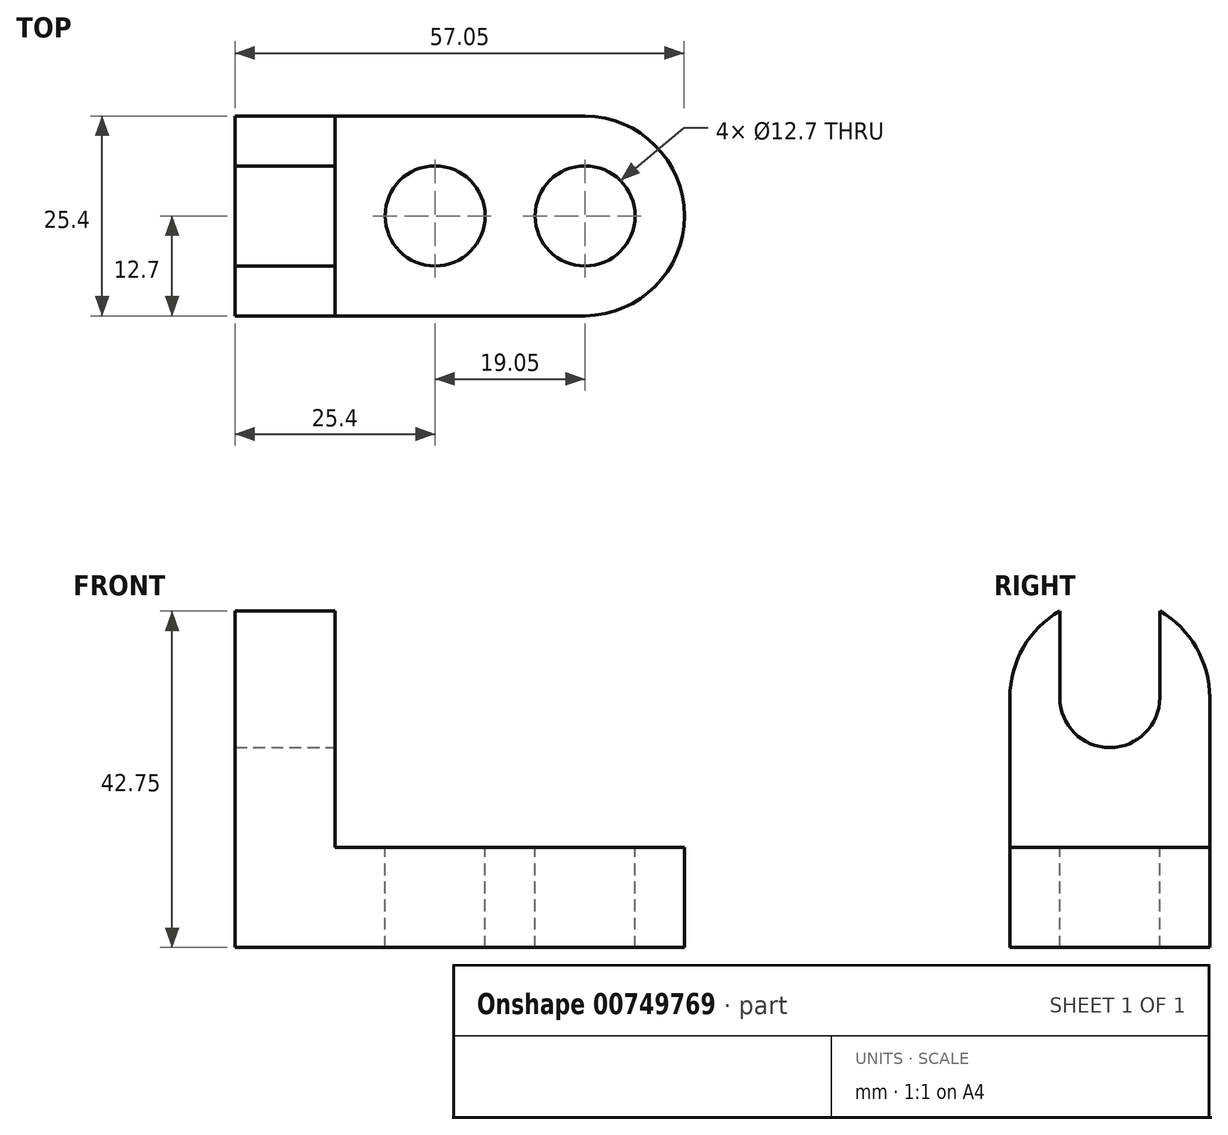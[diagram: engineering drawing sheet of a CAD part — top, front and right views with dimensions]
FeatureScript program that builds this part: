
annotation { "Feature Type Name" : "Feature", "Feature Type Description" : "" }
export const myFeature = defineFeature(function(context is Context, id is Id, definition is map)
    precondition{}
    {
        {
            var Q0;
            Q0=qCreatedBy(makeId("Front.planeOp"),FACE);
            var sketch = newSketch(context, id + "F0", { "sketchPlane" : qUnion([Q0])});
            skLineSegment(sketch, "E0", {"start": v(0, 0) * mm, "end": v(57.15, 0) * mm});
            skLineSegment(sketch, "E1", {"start": v(57.15, 0) * mm, "end": v(57.15, 12.7) * mm});
            skLineSegment(sketch, "E2", {"start": v(57.15, 12.7) * mm, "end": v(12.7, 12.7) * mm});
            skLineSegment(sketch, "E3", {"start": v(12.7, 12.7) * mm, "end": v(12.7, 44.45) * mm});
            skLineSegment(sketch, "E4", {"start": v(12.7, 44.45) * mm, "end": v(0, 44.45) * mm});
            skLineSegment(sketch, "E5", {"start": v(0, 44.45) * mm, "end": v(0, 0) * mm});
            skSolve(sketch);
        }
        {
            var Q0;
            Q0=makeQuery(id+"F0.imprint","IMPRINT",FACE,{"disambiguationData":[TD([[makeQuery(id+"F0.imprint","IMPRINT",EDGE,{"derivedFrom":sQuery(id+"F0.wireOp",EDGE,"E0")}),1.0]])]});
            extrude(context, id + "F1", {"entities" : qUnion([Q0]), "depth" : 25.4 * mm, "offsetDistance" : 25.4 * mm});
        }
        {
            var Q0;
            Q0=makeQuery(id+"F1.opExtrude","SWEPT_FACE",FACE,{"disambiguationData":[OSD([sQuery(id+"F0.wireOp",EDGE,"E2")])]});
            var sketch = newSketch(context, id + "F2", { "sketchPlane" : qUnion([Q0])});
            skLineSegment(sketch, "E6", {"start": v(44.45, 0) * mm, "end": v(44.45, -25.4) * mm});
            skLineSegment(sketch, "E7", {"start": v(25.4, 0) * mm, "end": v(25.4, -25.4) * mm});
            skCircle(sketch, "E8", {"center": v(25.4, -12.7) * mm, "radius": 6.35 * mm});
            skCircle(sketch, "E9", {"center": v(44.45, -12.7) * mm, "radius": 6.35 * mm});
            skLineSegment(sketch, "E10", {"start": v(25.4, -6.35) * mm, "end": v(44.45, -6.35) * mm});
            skLineSegment(sketch, "E11", {"start": v(25.4, -19.05) * mm, "end": v(44.45, -19.05) * mm});
            skArc(sketch, "E12", {"start": v(44.45, -25.4) * mm, "mid": v(57.05, -12.7) * mm, "end": v(44.45, 0) * mm});
            skSolve(sketch);
        }
        {
            var Q0;
            {var subQ0=sQuery(id+"F2.wireOp",EDGE,"E8");var subQ1=sQuery(id+"F2.wireOp",EDGE,"E7");var subQ2=makeQuery(id+"F2.imprint","INTERSECT",VERTEX,{"derivedFrom":[subQ1,subQ0,sQuery(id+"F2.wireOp",EDGE,"E10")]});Q0=makeQuery(id+"F2.imprint","IMPRINT",FACE,{"disambiguationData":[TD([[makeQuery(id+"F2.imprint","IMPRINT",EDGE,{"disambiguationData":[TD([[subQ2,-1.0]])],"derivedFrom":subQ1}),-1.0]])]});}
            var Q1;
            {var subQ0=sQuery(id+"F2.wireOp",EDGE,"E8");var subQ1=sQuery(id+"F2.wireOp",EDGE,"E7");var subQ2=makeQuery(id+"F2.imprint","INTERSECT",VERTEX,{"derivedFrom":[subQ1,subQ0,sQuery(id+"F2.wireOp",EDGE,"E10")]});Q1=makeQuery(id+"F2.imprint","IMPRINT",FACE,{"disambiguationData":[TD([[makeQuery(id+"F2.imprint","IMPRINT",EDGE,{"disambiguationData":[TD([[subQ2,-1.0]])],"derivedFrom":subQ1}),1.0]])]});}
            var Q2;
            {var subQ0=sQuery(id+"F2.wireOp",EDGE,"E9");var subQ1=sQuery(id+"F2.wireOp",EDGE,"E6");var subQ2=makeQuery(id+"F2.imprint","INTERSECT",VERTEX,{"derivedFrom":[subQ1,subQ0,sQuery(id+"F2.wireOp",EDGE,"E10")]});Q2=makeQuery(id+"F2.imprint","IMPRINT",FACE,{"disambiguationData":[TD([[makeQuery(id+"F2.imprint","IMPRINT",EDGE,{"disambiguationData":[TD([[subQ2,-1.0]])],"derivedFrom":subQ1}),-1.0]])]});}
            var Q3;
            {var subQ0=sQuery(id+"F2.wireOp",EDGE,"E9");var subQ1=sQuery(id+"F2.wireOp",EDGE,"E6");var subQ2=makeQuery(id+"F2.imprint","INTERSECT",VERTEX,{"derivedFrom":[subQ1,subQ0,sQuery(id+"F2.wireOp",EDGE,"E10")]});Q3=makeQuery(id+"F2.imprint","IMPRINT",FACE,{"disambiguationData":[TD([[makeQuery(id+"F2.imprint","IMPRINT",EDGE,{"disambiguationData":[TD([[subQ2,-1.0]])],"derivedFrom":subQ1}),1.0]])]});}
            var Q4;
            {var subQ0=sQuery(id+"F2.wireOp",EDGE,"E12");Q4=makeQuery(id+"F2.imprint","IMPRINT",FACE,{"disambiguationData":[TD([[makeQuery(id+"F2.imprint","IMPRINT",EDGE,{"derivedFrom":subQ0}),-1.0]])]});}
            extrude(context, id + "F3", {"entities" : qUnion([Q0, Q1, Q2, Q3, Q4]), "operationType" : NewBodyOperationType.REMOVE, "endBound" : BoundingType.THROUGH_ALL, "oppositeDirection" : true, "depth" : 25.4 * mm, "offsetDistance" : 25.4 * mm});
        }
        {
            var Q0;
            Q0=makeQuery(id+"F1.opExtrude","SWEPT_FACE",FACE,{"disambiguationData":[OSD([sQuery(id+"F0.wireOp",EDGE,"E3")])]});
            var sketch = newSketch(context, id + "F4", { "sketchPlane" : qUnion([Q0])});
            skLineSegment(sketch, "E13", {"start": v(-25.4, 31.75) * mm, "end": v(0, 31.75) * mm});
            skCircle(sketch, "E14", {"center": v(-12.7, 31.75) * mm, "radius": 6.35 * mm});
            skLineSegment(sketch, "E15", {"start": v(-19.05, 44.45) * mm, "end": v(-19.05, 12.7) * mm});
            skLineSegment(sketch, "E16", {"start": v(-6.35, 44.45) * mm, "end": v(-6.35, 12.7) * mm});
            skArc(sketch, "E17", {"start": v(0, 31.75) * mm, "mid": v(-12.7, 44.45) * mm, "end": v(-25.4, 31.75) * mm});
            skSolve(sketch);
        }
        {
            var Q0;
            {var subQ0=sQuery(id+"F4.wireOp",EDGE,"E15");var subQ4=sQuery(id+"F4.wireOp",EDGE,"E17");var subQ5=makeQuery(id+"F4.imprint","INTERSECT",VERTEX,{"derivedFrom":[subQ0,subQ4]});Q0=makeQuery(id+"F4.imprint","IMPRINT",FACE,{"disambiguationData":[TD([[makeQuery(id+"F4.imprint","IMPRINT",EDGE,{"disambiguationData":[TD([[subQ5,1.0]])],"derivedFrom":subQ0}),-1.0]])]});}
            var Q1;
            {var subQ0=sQuery(id+"F4.wireOp",EDGE,"E16");var subQ4=sQuery(id+"F4.wireOp",EDGE,"E17");var subQ5=makeQuery(id+"F4.imprint","INTERSECT",VERTEX,{"derivedFrom":[subQ0,subQ4]});Q1=makeQuery(id+"F4.imprint","IMPRINT",FACE,{"disambiguationData":[TD([[makeQuery(id+"F4.imprint","IMPRINT",EDGE,{"disambiguationData":[TD([[subQ5,1.0]])],"derivedFrom":subQ0}),1.0]])]});}
            var Q2;
            {var subQ0=sQuery(id+"F4.wireOp",EDGE,"E14");var subQ1=sQuery(id+"F4.wireOp",EDGE,"E13");var subQ2=makeQuery(id+"F4.imprint","INTERSECT",VERTEX,{"derivedFrom":[subQ1,subQ0,sQuery(id+"F4.wireOp",EDGE,"E15")]});Q2=makeQuery(id+"F4.imprint","IMPRINT",FACE,{"disambiguationData":[TD([[makeQuery(id+"F4.imprint","IMPRINT",EDGE,{"disambiguationData":[TD([[subQ2,-1.0]])],"derivedFrom":subQ1}),-1.0]])]});}
            var Q3;
            {var subQ0=sQuery(id+"F4.wireOp",EDGE,"E14");var subQ1=sQuery(id+"F4.wireOp",EDGE,"E13");var subQ2=makeQuery(id+"F4.imprint","INTERSECT",VERTEX,{"derivedFrom":[subQ1,subQ0,sQuery(id+"F4.wireOp",EDGE,"E15")]});Q3=makeQuery(id+"F4.imprint","IMPRINT",FACE,{"disambiguationData":[TD([[makeQuery(id+"F4.imprint","IMPRINT",EDGE,{"disambiguationData":[TD([[subQ2,-1.0]])],"derivedFrom":subQ1}),1.0]])]});}
            var Q4;
            {var subQ0=sQuery(id+"F4.wireOp",EDGE,"E17");var subQ7=sQuery(id+"F4.wireOp",EDGE,"E15");var subQ8=makeQuery(id+"F4.imprint","INTERSECT",VERTEX,{"derivedFrom":[subQ7,subQ0]});Q4=makeQuery(id+"F4.imprint","IMPRINT",FACE,{"disambiguationData":[TD([[makeQuery(id+"F4.imprint","IMPRINT",EDGE,{"disambiguationData":[TD([[subQ8,-1.0]])],"derivedFrom":subQ7}),1.0]])]});}
            var Q5;
            {var subQ0=sQuery(id+"F4.wireOp",EDGE,"E16");var subQ3=sQuery(id+"F4.wireOp",EDGE,"E17");var subQ4=makeQuery(id+"F4.imprint","INTERSECT",VERTEX,{"derivedFrom":[subQ0,subQ3]});Q5=makeQuery(id+"F4.imprint","IMPRINT",FACE,{"disambiguationData":[TD([[makeQuery(id+"F4.imprint","IMPRINT",EDGE,{"disambiguationData":[TD([[subQ4,1.0]])],"derivedFrom":subQ0}),-1.0]])]});}
            var Q6;
            {var subQ0=sQuery(id+"F4.wireOp",EDGE,"E15");var subQ3=sQuery(id+"F4.wireOp",EDGE,"E17");var subQ4=makeQuery(id+"F4.imprint","INTERSECT",VERTEX,{"derivedFrom":[subQ0,subQ3]});Q6=makeQuery(id+"F4.imprint","IMPRINT",FACE,{"disambiguationData":[TD([[makeQuery(id+"F4.imprint","IMPRINT",EDGE,{"disambiguationData":[TD([[subQ4,1.0]])],"derivedFrom":subQ0}),1.0]])]});}
            extrude(context, id + "F5", {"entities" : qUnion([Q0, Q1, Q2, Q3, Q4, Q5, Q6]), "operationType" : NewBodyOperationType.REMOVE, "endBound" : BoundingType.THROUGH_ALL, "oppositeDirection" : true, "depth" : 25.4 * mm, "offsetDistance" : 25.4 * mm});
        }
    });
